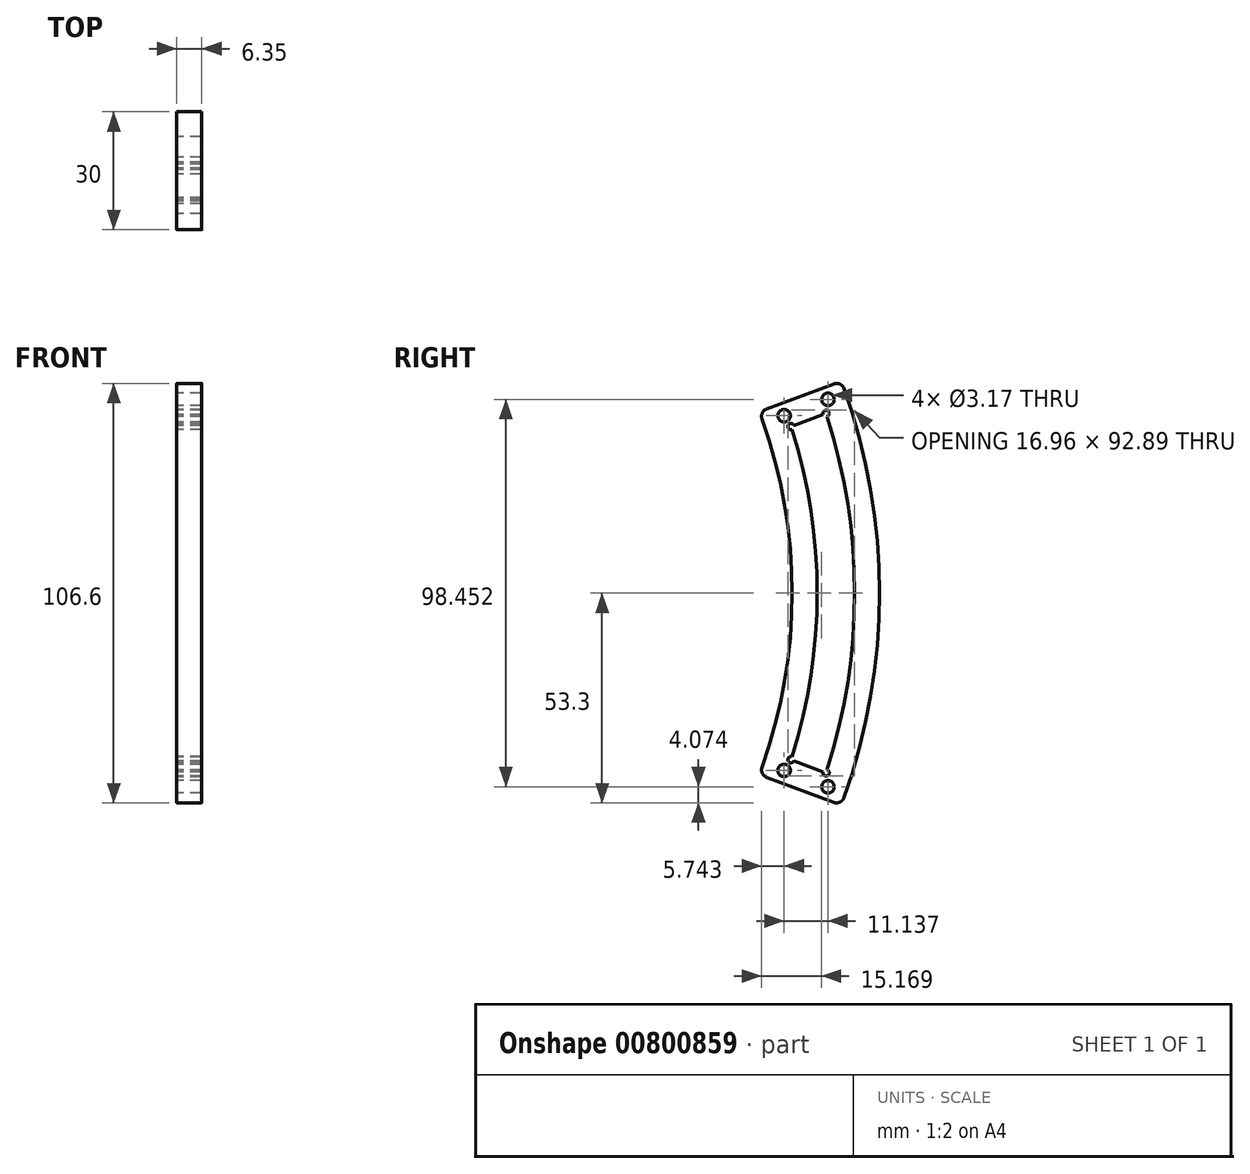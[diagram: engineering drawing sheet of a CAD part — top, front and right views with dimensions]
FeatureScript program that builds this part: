
annotation { "Feature Type Name" : "Feature", "Feature Type Description" : "" }
export const myFeature = defineFeature(function(context is Context, id is Id, definition is map)
    precondition{}
    {
        {
            var Q0;
            Q0=qCreatedBy(makeId("Right.planeOp"),FACE);
            var sketch = newSketch(context, id + "F0", { "sketchPlane" : qUnion([Q0])});
            skArc(sketch, "E0", {"start": v(133.84, 50) * mm, "mid": v(142.88, 0) * mm, "end": v(133.84, -50) * mm, "construction": true});
            skLineSegment(sketch, "E1", {"start": v(0, 0) * mm, "end": v(142.88, 0) * mm, "construction": true});
            skArc(sketch, "E2.0", {"start": v(131.7, 41.57) * mm, "mid": v(138.11, 0) * mm, "end": v(131.7, -41.57) * mm});
            skArc(sketch, "E3.0", {"start": v(140.64, 44.9) * mm, "mid": v(147.64, 0) * mm, "end": v(140.64, -44.9) * mm});
            skArc(sketch, "E4", {"start": v(124.1, 44.25) * mm, "mid": v(131.76, 0) * mm, "end": v(124.1, -44.25) * mm});
            skArc(sketch, "E5", {"start": v(144.95, -51.98) * mm, "mid": v(153.99, 0) * mm, "end": v(144.95, 51.98) * mm});
            skLineSegment(sketch, "E6", {"start": v(142.37, 53.17) * mm, "end": v(125.3, 46.8) * mm});
            skPoint(sketch, "E7.orphan", {"position": v(0, 131.76) * mm});
            skPoint(sketch, "E8.orphan", {"position": v(0, 142.88) * mm});
            skPoint(sketch, "E9.orphan", {"position": v(0, 153.99) * mm});
            skLineSegment(sketch, "E10.MirrorCS", {"start": v(142.37, -53.17) * mm, "end": v(125.3, -46.8) * mm});
            skLineSegment(sketch, "E11.trimOffspring", {"start": v(139.66, 45.38) * mm, "end": v(132.21, 42.6) * mm});
            skPoint(sketch, "E12.orphan", {"position": v(0, -131.76) * mm});
            skPoint(sketch, "E13.orphan", {"position": v(0, -142.88) * mm});
            skPoint(sketch, "E14.orphan", {"position": v(0, -147.64) * mm});
            skPoint(sketch, "E15.orphan", {"position": v(0, -153.99) * mm});
            skPoint(sketch, "E16.trimOffspring.end.orphan", {"position": v(125.66, -40.15) * mm});
            skLineSegment(sketch, "E17.trimOffspring", {"start": v(139.66, -45.38) * mm, "end": v(132.21, -42.6) * mm});
            skPoint(sketch, "E18.orphan", {"position": v(125.66, 40.15) * mm});
            skCircle(sketch, "E19", {"center": v(129.73, 45.07) * mm, "radius": 1.59 * mm});
            skCircle(sketch, "E20", {"center": v(140.87, 49.23) * mm, "radius": 1.59 * mm});
            skCircle(sketch, "E21.MirrorC", {"center": v(129.73, -45.07) * mm, "radius": 1.59 * mm});
            skCircle(sketch, "E22.MirrorC", {"center": v(140.87, -49.23) * mm, "radius": 1.59 * mm});
            skArc(sketch, "E23", {"start": v(139.66, -45.38) * mm, "mid": v(140.75, -46.38) * mm, "end": v(140.64, -44.9) * mm});
            skArc(sketch, "E24", {"start": v(131.7, -41.57) * mm, "mid": v(130.75, -42.67) * mm, "end": v(132.21, -42.6) * mm});
            skArc(sketch, "E25", {"start": v(132.21, 42.6) * mm, "mid": v(130.75, 42.67) * mm, "end": v(131.7, 41.57) * mm});
            skArc(sketch, "E26", {"start": v(140.64, 44.9) * mm, "mid": v(140.75, 46.38) * mm, "end": v(139.66, 45.38) * mm});
            skPoint(sketch, "E27.visualSharp", {"position": v(123.43, 46.1) * mm});
            skArc(sketch, "E27.filletArc", {"start": v(125.3, 46.8) * mm, "mid": v(124.18, 45.77) * mm, "end": v(124.1, 44.25) * mm});
            skPoint(sketch, "E28.visualSharp", {"position": v(144.25, 53.88) * mm});
            skArc(sketch, "E28.filletArc", {"start": v(144.95, 51.98) * mm, "mid": v(143.9, 53.12) * mm, "end": v(142.37, 53.17) * mm});
            skPoint(sketch, "E29.visualSharp", {"position": v(123.43, -46.1) * mm});
            skArc(sketch, "E29.filletArc", {"start": v(124.1, -44.25) * mm, "mid": v(124.18, -45.77) * mm, "end": v(125.3, -46.8) * mm});
            skPoint(sketch, "E30.visualSharp", {"position": v(144.25, -53.88) * mm});
            skArc(sketch, "E30.filletArc", {"start": v(142.37, -53.17) * mm, "mid": v(143.9, -53.12) * mm, "end": v(144.95, -51.98) * mm});
            skSolve(sketch);
        }
        {
            var Q0;
            Q0 = qSketchRegion(id + "F0", true);
            extrude(context, id + "F1", {"entities" : qUnion([Q0]), "depth" : 6.35 * mm, "offsetDistance" : 25 * mm});
        }
    });
